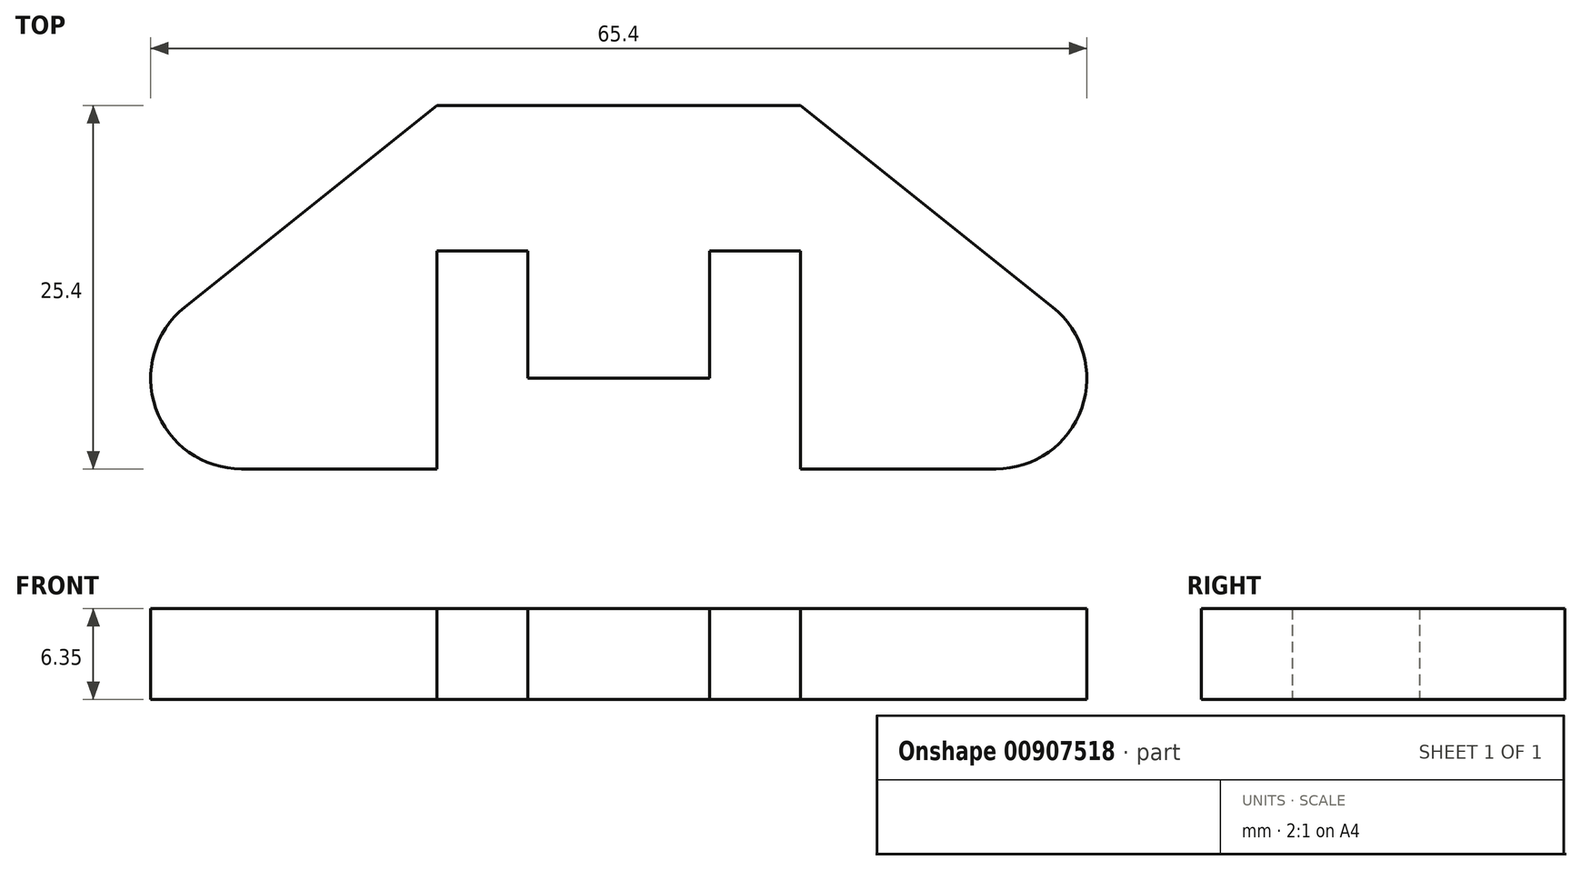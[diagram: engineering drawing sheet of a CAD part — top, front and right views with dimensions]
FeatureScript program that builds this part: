
annotation { "Feature Type Name" : "Feature", "Feature Type Description" : "" }
export const myFeature = defineFeature(function(context is Context, id is Id, definition is map)
    precondition{}
    {
        {
            var Q0;
            Q0=qCreatedBy(makeId("Top.planeOp"),FACE);
            var sketch = newSketch(context, id + "F0", { "sketchPlane" : qUnion([Q0])});
            skLineSegment(sketch, "E0", {"start": v(-26.35, 0) * mm, "end": v(-12.7, 0) * mm});
            skLineSegment(sketch, "E1", {"start": v(30.31, 11.3) * mm, "end": v(12.7, 25.4) * mm});
            skLineSegment(sketch, "E2", {"start": v(12.7, 25.4) * mm, "end": v(-12.7, 25.4) * mm});
            skLineSegment(sketch, "E3", {"start": v(-12.7, 25.4) * mm, "end": v(-30.31, 11.3) * mm});
            skPoint(sketch, "E4.visualSharp", {"position": v(-44.45, 0) * mm});
            skArc(sketch, "E4.filletArc", {"start": v(-30.31, 11.3) * mm, "mid": v(-32.34, 4.25) * mm, "end": v(-26.35, 0) * mm});
            skPoint(sketch, "E5.visualSharp", {"position": v(44.45, 0) * mm});
            skArc(sketch, "E5.filletArc", {"start": v(26.35, 0) * mm, "mid": v(32.34, 4.25) * mm, "end": v(30.31, 11.3) * mm});
            skLineSegment(sketch, "E6.bottom", {"start": v(-12.7, 15.24) * mm, "end": v(-6.35, 15.24) * mm});
            skLineSegment(sketch, "E6.left", {"start": v(-12.7, 15.24) * mm, "end": v(-12.7, 0) * mm});
            skLineSegment(sketch, "E6.right", {"start": v(-6.35, 15.24) * mm, "end": v(-6.35, 6.35) * mm});
            skLineSegment(sketch, "E7.bottom", {"start": v(12.7, 15.24) * mm, "end": v(6.35, 15.24) * mm});
            skLineSegment(sketch, "E7.left", {"start": v(12.7, 15.24) * mm, "end": v(12.7, 0) * mm});
            skLineSegment(sketch, "E7.right", {"start": v(6.35, 15.24) * mm, "end": v(6.35, 6.35) * mm});
            skLineSegment(sketch, "E8.trimOffspring", {"start": v(12.7, 0) * mm, "end": v(26.35, 0) * mm});
            skLineSegment(sketch, "E9.trimOffspring", {"start": v(-6.35, 0) * mm, "end": v(6.35, 0) * mm, "construction": true});
            skLineSegment(sketch, "E10", {"start": v(6.35, 6.35) * mm, "end": v(-6.35, 6.35) * mm});
            skLineSegment(sketch, "E11", {"start": v(6.35, 6.35) * mm, "end": v(6.35, 0) * mm, "construction": true});
            skLineSegment(sketch, "E12", {"start": v(-6.35, 6.35) * mm, "end": v(-6.35, 6.35) * mm});
            skLineSegment(sketch, "E13", {"start": v(-6.35, 6.35) * mm, "end": v(-6.35, 0) * mm, "construction": true});
            skSolve(sketch);
        }
        {
            var Q0;
            Q0 = qSketchRegion(id + "F0", true);
            extrude(context, id + "F1", {"entities" : qUnion([Q0]), "depth" : 6.35 * mm, "offsetDistance" : 25.4 * mm});
        }
    });
